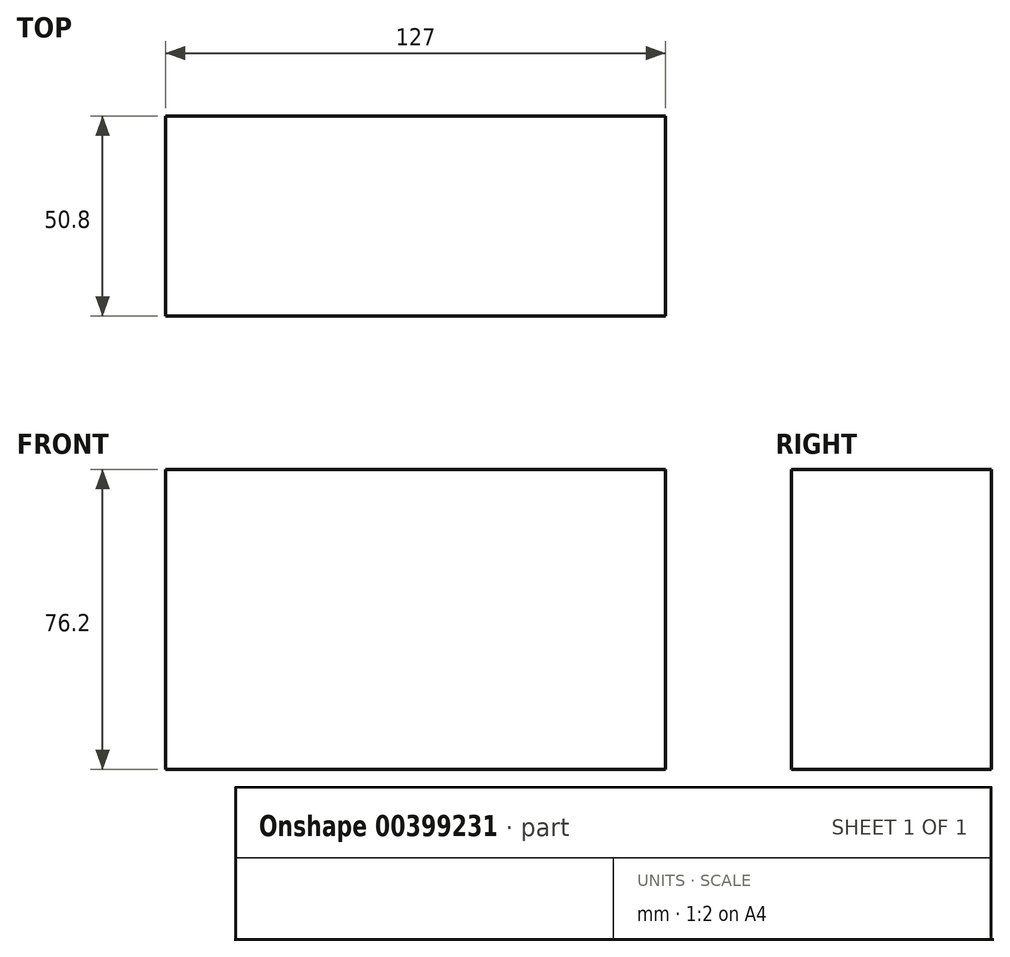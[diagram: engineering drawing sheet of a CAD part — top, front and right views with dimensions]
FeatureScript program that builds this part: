
annotation { "Feature Type Name" : "Feature", "Feature Type Description" : "" }
export const myFeature = defineFeature(function(context is Context, id is Id, definition is map)
    precondition{}
    {
        {
            var Q0;
            Q0=qCreatedBy(makeId("Front.planeOp"),FACE);
            var sketch = newSketch(context, id + "F0", { "sketchPlane" : qUnion([Q0])});
            skLineSegment(sketch, "E0.bottom", {"start": v(63.5, 38.1) * mm, "end": v(-63.5, 38.1) * mm});
            skLineSegment(sketch, "E0.top", {"start": v(63.5, -38.1) * mm, "end": v(-63.5, -38.1) * mm});
            skLineSegment(sketch, "E0.left", {"start": v(63.5, 38.1) * mm, "end": v(63.5, -38.1) * mm});
            skLineSegment(sketch, "E0.right", {"start": v(-63.5, 38.1) * mm, "end": v(-63.5, -38.1) * mm});
            skPoint(sketch, "E0.middle", {"position": v(0, 0) * mm});
            skSolve(sketch);
        }
        {
            var Q0;
            Q0 = qSketchRegion(id + "F0", true);
            extrude(context, id + "F1", {"entities" : qUnion([Q0]), "endBound" : BoundingType.SYMMETRIC, "depth" : 50.8 * mm});
        }
    });
